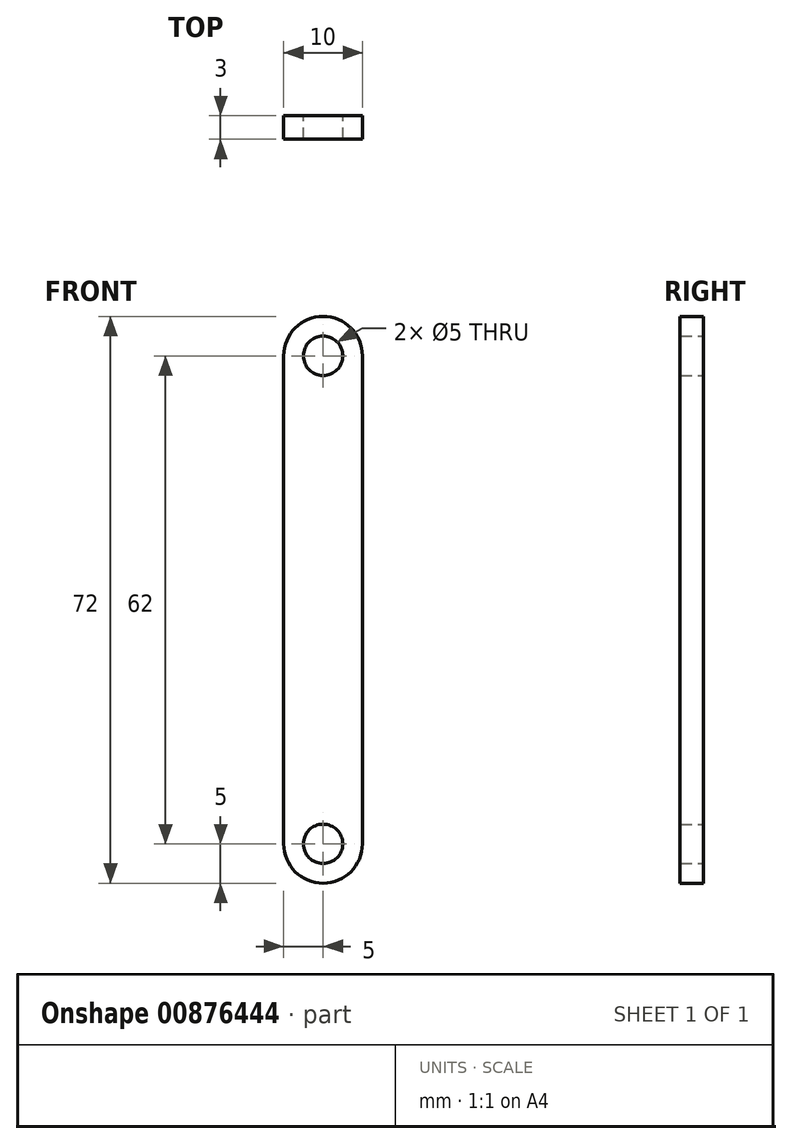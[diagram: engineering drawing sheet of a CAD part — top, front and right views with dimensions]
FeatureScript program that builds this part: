
annotation { "Feature Type Name" : "Feature", "Feature Type Description" : "" }
export const myFeature = defineFeature(function(context is Context, id is Id, definition is map)
    precondition{}
    {
        {
            var Q0;
            Q0=qCreatedBy(makeId("Front.planeOp"),FACE);
            var sketch = newSketch(context, id + "F0", { "sketchPlane" : qUnion([Q0])});
            skLineSegment(sketch, "E0.left", {"start": v(5, 31) * mm, "end": v(5, -31) * mm});
            skLineSegment(sketch, "E0.right", {"start": v(-5, 31) * mm, "end": v(-5, -31) * mm});
            skPoint(sketch, "E0.middle", {"position": v(0, 0) * mm});
            skArc(sketch, "E1", {"start": v(5, 31) * mm, "mid": v(0, 36) * mm, "end": v(-5, 31) * mm});
            skArc(sketch, "E2", {"start": v(-5, -31) * mm, "mid": v(0, -36) * mm, "end": v(5, -31) * mm});
            skCircle(sketch, "E3", {"center": v(0, 31) * mm, "radius": 2.5 * mm});
            skCircle(sketch, "E4", {"center": v(0, -31) * mm, "radius": 2.5 * mm});
            skSolve(sketch);
        }
        {
            var Q0;
            Q0 = qSketchRegion(id + "F0", true);
            extrude(context, id + "F1", {"entities" : qUnion([Q0]), "depth" : 3 * mm, "offsetDistance" : 25 * mm});
        }
    });
